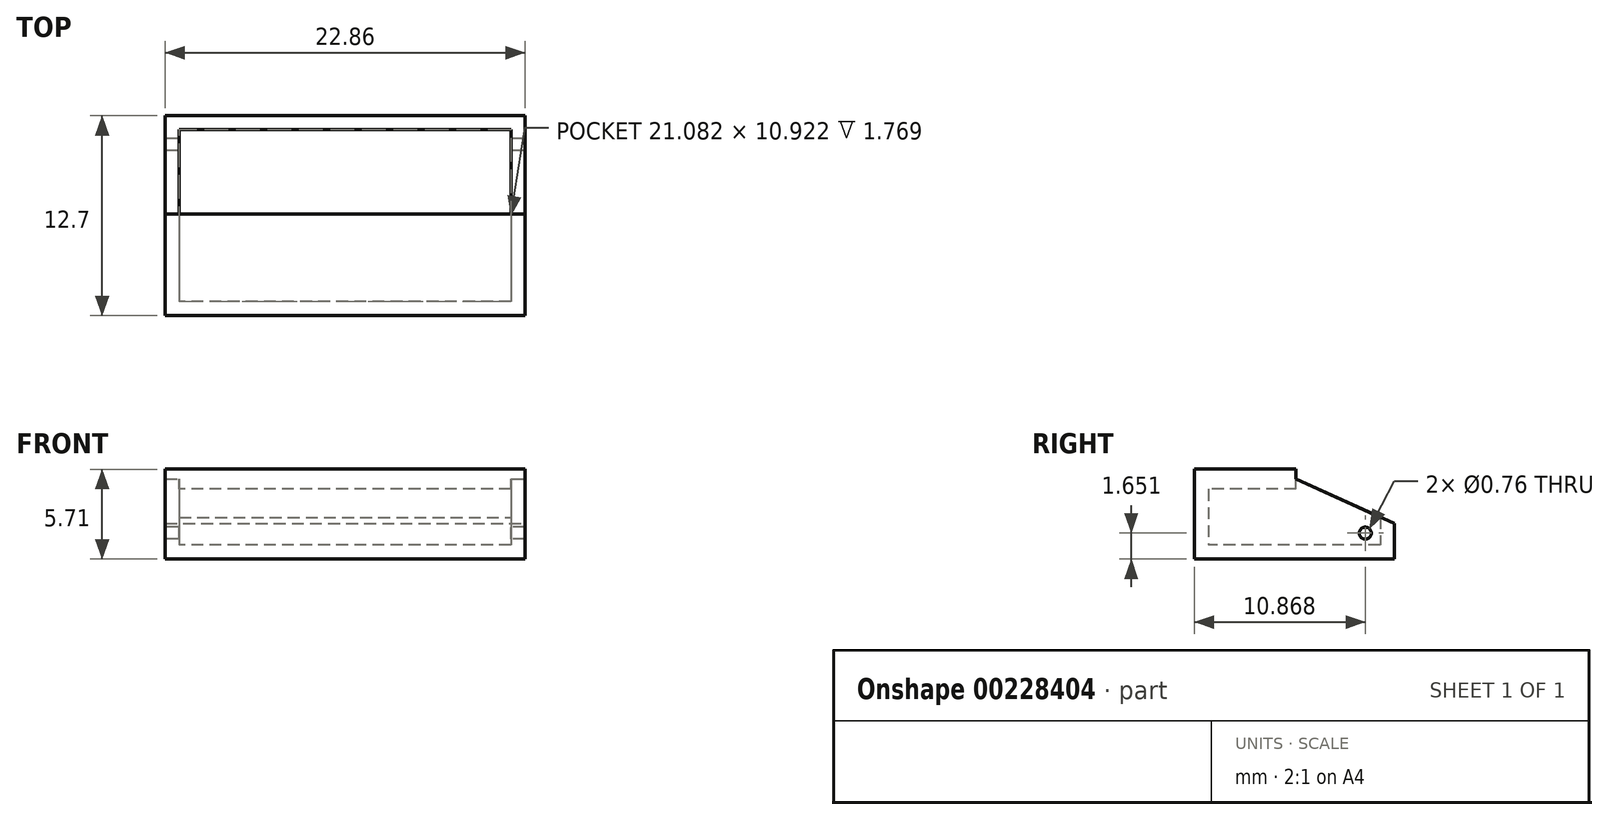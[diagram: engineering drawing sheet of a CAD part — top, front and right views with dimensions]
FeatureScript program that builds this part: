
annotation { "Feature Type Name" : "Feature", "Feature Type Description" : "" }
export const myFeature = defineFeature(function(context is Context, id is Id, definition is map)
    precondition{}
    {
        {
            var Q0;
            Q0=qCreatedBy(makeId("Top.planeOp"),FACE);
            var sketch = newSketch(context, id + "F0", { "sketchPlane" : qUnion([Q0])});
            skLineSegment(sketch, "E0.bottom", {"start": v(11.43, 6.35) * mm, "end": v(-11.43, 6.35) * mm});
            skLineSegment(sketch, "E0.top", {"start": v(11.43, -6.35) * mm, "end": v(-11.43, -6.35) * mm});
            skLineSegment(sketch, "E0.left", {"start": v(11.43, 6.35) * mm, "end": v(11.43, -6.35) * mm});
            skLineSegment(sketch, "E0.right", {"start": v(-11.43, 6.35) * mm, "end": v(-11.43, -6.35) * mm});
            skPoint(sketch, "E0.middle", {"position": v(0, 0) * mm});
            skSolve(sketch);
        }
        {
            var Q0;
            Q0 = qSketchRegion(id + "F0", true);
            extrude(context, id + "F1", {"entities" : qUnion([Q0]), "depth" : 5.08 * mm});
        }
        {
            var Q0;
            Q0=makeQuery(id+"F1.opExtrude","CAP_FACE",FACE,{"disambiguationData":[OSD([sQuery(id+"F0.wireOp",EDGE,"E0.bottom"),sQuery(id+"F0.wireOp",EDGE,"E0.top"),sQuery(id+"F0.wireOp",EDGE,"E0.left"),sQuery(id+"F0.wireOp",EDGE,"E0.right")])],"isStart":false});
            shell(context, id + "F2", {"entities" : qUnion([Q0]), "thickness" : 0.89 * mm});
        }
        {
            var Q0;
            Q0=qCreatedBy(makeId("Right.planeOp"),FACE);
            var sketch = newSketch(context, id + "F3", { "sketchPlane" : qUnion([Q0])});
            skLineSegment(sketch, "E1", {"start": v(6.35, 2.25) * mm, "end": v(0, 5.13) * mm});
            skLineSegment(sketch, "E2", {"start": v(0, 5.13) * mm, "end": v(6.91, 6.37) * mm});
            skLineSegment(sketch, "E3", {"start": v(6.91, 6.37) * mm, "end": v(7.29, 2.14) * mm});
            skLineSegment(sketch, "E4", {"start": v(7.29, 2.14) * mm, "end": v(6.35, 2.25) * mm});
            skSolve(sketch);
        }
        {
            var Q0;
            Q0 = qSketchRegion(id + "F3", true);
            extrude(context, id + "F4", {"entities" : qUnion([Q0]), "operationType" : NewBodyOperationType.REMOVE, "endBound" : BoundingType.THROUGH_ALL, "depth" : 25.4 * mm, "hasSecondDirection" : true, "secondDirectionOppositeDirection" : true, "secondDirectionDepth" : 25.4 * mm});
        }
        {
            var Q0;
            Q0=makeQuery(id+"F1.opExtrude","CAP_FACE",FACE,{"disambiguationData":[OSD([sQuery(id+"F0.wireOp",EDGE,"E0.bottom"),sQuery(id+"F0.wireOp",EDGE,"E0.top"),sQuery(id+"F0.wireOp",EDGE,"E0.left"),sQuery(id+"F0.wireOp",EDGE,"E0.right")])],"isStart":false});
            var sketch = newSketch(context, id + "F5", { "sketchPlane" : qUnion([Q0])});
            skLineSegment(sketch, "E5.bottom", {"start": v(-11.43, 0.12) * mm, "end": v(11.43, 0.12) * mm});
            skLineSegment(sketch, "E5.top", {"start": v(-11.43, -6.35) * mm, "end": v(11.43, -6.35) * mm});
            skLineSegment(sketch, "E5.left", {"start": v(-11.43, 0.12) * mm, "end": v(-11.43, -6.35) * mm});
            skLineSegment(sketch, "E5.right", {"start": v(11.43, 0.12) * mm, "end": v(11.43, -6.35) * mm});
            skSolve(sketch);
        }
        {
            var Q0;
            Q0 = qSketchRegion(id + "F5", true);
            extrude(context, id + "F6", {"entities" : qUnion([Q0]), "operationType" : NewBodyOperationType.ADD, "depth" : 0.64 * mm, "hasSecondDirection" : true, "secondDirectionOppositeDirection" : true, "secondDirectionDepth" : 0.64 * mm});
        }
        {
            var Q0;
            Q0=makeQuery(id+"F6.boolean.opBoolean","MERGE",FACE,{"derivedFrom":[makeQuery(id+"F1.opExtrude","SWEPT_FACE",FACE,{"disambiguationData":[OSD([sQuery(id+"F0.wireOp",EDGE,"E0.right")])]}),makeQuery(id+"F6.opExtrude","SWEPT_FACE",FACE,{"disambiguationData":[OSD([sQuery(id+"F5.wireOp",EDGE,"E5.left")])]})]});
            var sketch = newSketch(context, id + "F7", { "sketchPlane" : qUnion([Q0])});
            skCircle(sketch, "E6", {"center": v(-4.52, 1.65) * mm, "radius": 0.38 * mm});
            skSolve(sketch);
        }
        {
            var Q0;
            Q0 = qSketchRegion(id + "F7", true);
            extrude(context, id + "F8", {"entities" : qUnion([Q0]), "operationType" : NewBodyOperationType.REMOVE, "endBound" : BoundingType.THROUGH_ALL, "oppositeDirection" : true, "depth" : 25.4 * mm});
        }
    });
